# Revit family: Desks-Teknion-B_RTD_Rectangular_Table-R2019
name_source: partatom
category: Furniture
units: mm (PartAtom-declared; Revit-internal decimal feet)

## family parameters
Always vertical = Yes
Cut with Voids When Loaded = No
OmniClass Number = 23.40.20.00
OmniClass Title = General Furniture and Specialties
Room Calculation Point = No
Shared = Yes
Work Plane-Based = No

## types (6) — shared parameters
Assembly Code = E2020200
Manufacturer = Teknion
Manufacturer Fax = 416.661.4586
Part Number = B_RTD
Product Documentation Link = https://www.teknion.com
Product Documentation Link #2 = https://www.teknion.com
Product Documentation Link #3 = https://www.teknion.com
Product Documentation Link #4 = https://www.teknion.com
Product Documentation Link #5 = https://www.teknion.com
Product Line = Expansion Casegoods
Product Page URL = http://www.teknion.com
Series = Expansion Casegoods
Sustainability Data = http://www.teknion.com
URL = www.teknion.com
Unit Weight URL = http://www.teknion.com
Warranty = http://www.teknion.com

## per-type parameters (varying)
| type | 1" WS | 1-3/16" WS | 1-9/16" WS | Angular Leg | Blade Leg | Description | Model | Thickness |
| 1-3/16" Worksurface Thickness, Angular Leg | No | Yes | No | Yes | No | Rectangular Table, 1-3/16" Worksurface Thickness, Angular Leg | BMRTDA_____ | 1.189 " |
| 1" Worksurface Thickness, Angular Leg | Yes | No | No | Yes | No | Rectangular Table, 1" Worksurface Thickness, Angular Leg | BDRTDA_____ | 1.016 " |
| 1-9/16" Worksurface Thickness, Angular Leg | No | No | Yes | Yes | No | Rectangular Table, 1-9/16" Worksurface Thickness, Angular Leg | BXRTDA_____ | 1.555 " |
| 1" Worksurface Thickness, Blade Leg | Yes | No | No | No | Yes | Rectangular Table, 1" Worksurface Thickness, Blade Leg | BDRTDK_____ | 1.016 " |
| 1-3/16" Worksurface Thickness, Blade Leg | No | Yes | No | No | Yes | Rectangular Table, 1-3/16" Worksurface Thickness, Blade Leg | BMRTDK_____ | 1.189 " |
| 1-9/16" Worksurface Thickness, Blade Leg | No | No | Yes | No | Yes | Rectangular Table, 1-9/16" Worksurface Thickness, Blade Leg | BXRTDK_____ | 1.555 " |

## geometry (parser evidence)
native form markers: Blend x25, Sweep x7
no freeform markers — native parametric forms only
